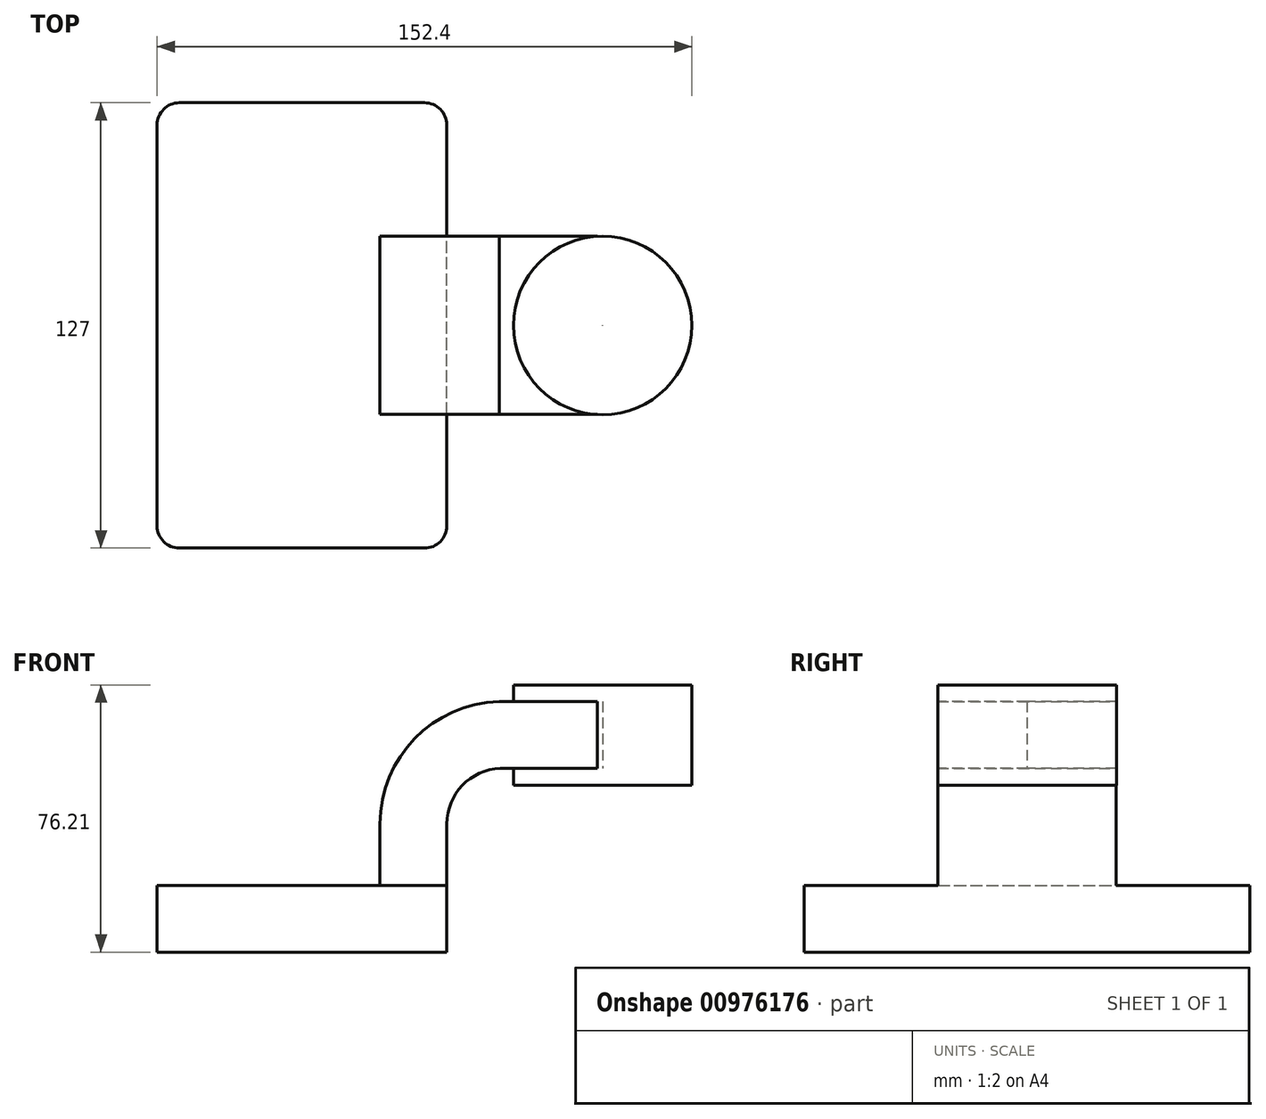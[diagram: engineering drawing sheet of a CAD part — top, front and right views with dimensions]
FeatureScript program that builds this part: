
annotation { "Feature Type Name" : "Feature", "Feature Type Description" : "" }
export const myFeature = defineFeature(function(context is Context, id is Id, definition is map)
    precondition{}
    {
        {
            var Q0;
            Q0=qCreatedBy(makeId("Front.planeOp"),FACE);
            var sketch = newSketch(context, id + "F0", { "sketchPlane" : qUnion([Q0])});
            skLineSegment(sketch, "E0.bottom", {"start": v(41.28, -9.52) * mm, "end": v(-41.27, -9.53) * mm});
            skLineSegment(sketch, "E0.top", {"start": v(41.27, 9.53) * mm, "end": v(-41.28, 9.53) * mm});
            skLineSegment(sketch, "E0.left", {"start": v(41.28, -9.52) * mm, "end": v(41.28, 9.53) * mm});
            skLineSegment(sketch, "E0.right", {"start": v(-41.27, -9.53) * mm, "end": v(-41.28, 9.53) * mm});
            skPoint(sketch, "E0.middle", {"position": v(0, 0) * mm});
            skLineSegment(sketch, "E1.bottom", {"start": v(111.12, 38.1) * mm, "end": v(60.32, 38.1) * mm});
            skLineSegment(sketch, "E1.top", {"start": v(111.12, 66.68) * mm, "end": v(60.32, 66.68) * mm});
            skLineSegment(sketch, "E1.left", {"start": v(111.12, 38.1) * mm, "end": v(111.12, 66.68) * mm});
            skLineSegment(sketch, "E1.right", {"start": v(60.32, 38.1) * mm, "end": v(60.32, 66.68) * mm});
            skPoint(sketch, "E1.middle", {"position": v(85.72, 52.39) * mm});
            skLineSegment(sketch, "E2", {"start": v(41.27, 9.53) * mm, "end": v(41.27, 27.01) * mm});
            skArc(sketch, "E3", {"start": v(41.27, 27.01) * mm, "mid": v(45.7, 38) * mm, "end": v(56.49, 42.88) * mm});
            skLineSegment(sketch, "E4", {"start": v(56.49, 42.88) * mm, "end": v(85.71, 42.88) * mm});
            skLineSegment(sketch, "E5.0", {"start": v(56.17, 61.93) * mm, "end": v(85.71, 61.93) * mm});
            skArc(sketch, "E5.1", {"start": v(22.23, 27.01) * mm, "mid": v(32.1, 51.36) * mm, "end": v(56.17, 61.93) * mm});
            skLineSegment(sketch, "E5.2", {"start": v(22.23, 9.53) * mm, "end": v(22.23, 27.01) * mm});
            skLineSegment(sketch, "E6", {"start": v(85.71, 42.88) * mm, "end": v(85.71, 61.93) * mm});
            skFitSpline(sketch, "E7", {"points": [v(-41.28, 9.53) * mm, v(56.17, 61.93) * mm], "startDerivative": vector(1.72, 146.9) * mm, "endDerivative": vector(113.51, -5.56) * mm});
            skLineSegment(sketch, "E8", {"start": v(85.68, 38.1) * mm, "end": v(85.68, 66.68) * mm});
            skSolve(sketch);
        }
        {
            var Q0;
            Q0=makeQuery(id+"F0.imprint","IMPRINT",FACE,{"disambiguationData":[TD([[makeQuery(id+"F0.imprint","IMPRINT",EDGE,{"derivedFrom":sQuery(id+"F0.wireOp",EDGE,"E0.bottom")}),-1.0]])]});
            extrude(context, id + "F1", {"entities" : qUnion([Q0]), "endBound" : BoundingType.SYMMETRIC, "depth" : 127 * mm, "offsetDistance" : 25.4 * mm});
        }
        {
            var Q0;
            {var subQ1=sQuery(id+"F0.wireOp",EDGE,"E2");Q0=makeQuery(id+"F0.imprint","IMPRINT",FACE,{"disambiguationData":[TD([[makeQuery(id+"F0.imprint","IMPRINT",EDGE,{"derivedFrom":subQ1}),1.0]])]});}
            extrude(context, id + "F2", {"entities" : qUnion([Q0]), "operationType" : NewBodyOperationType.ADD, "endBound" : BoundingType.SYMMETRIC, "depth" : 50.8 * mm, "offsetDistance" : 25.4 * mm});
        }
        {
            var Q0;
            Q0=makeQuery(id+"F0.imprint","IMPRINT",FACE,{"disambiguationData":[TD([[makeQuery(id+"F0.imprint","IMPRINT",EDGE,{"derivedFrom":sQuery(id+"F0.wireOp",EDGE,"E5.1")}),1.0]])]});
            extrude(context, id + "F3", {"entities" : qUnion([Q0]), "operationType" : NewBodyOperationType.ADD, "endBound" : BoundingType.SYMMETRIC, "depth" : 15.88 * mm, "offsetDistance" : 25.4 * mm});
        }
        {
            var Q0;
            {var subQ0=sQuery(id+"F0.wireOp",EDGE,"E1.left");Q0=makeQuery(id+"F0.imprint","IMPRINT",FACE,{"disambiguationData":[TD([[makeQuery(id+"F0.imprint","IMPRINT",EDGE,{"derivedFrom":subQ0}),1.0]])]});}
            var Q1;
            Q1=sQuery(id+"F0.wireOp",EDGE,"E8");
            revolve(context, id + "F4", {"operationType" : NewBodyOperationType.ADD, "surfaceOperationType" : NewSurfaceOperationType.NEW, "entities" : qUnion([Q0]), "axis" : qUnion([Q1]), "revolveType" : RevolveType.FULL});
        }
        {
            var Q0;
            {var subQ0=sQuery(id+"F0.wireOp",EDGE,"E4");var subQ1=sQuery(id+"F0.wireOp",EDGE,"E1.right");var subQ2=makeQuery(id+"F0.imprint","INTERSECT",VERTEX,{"derivedFrom":[subQ1,subQ0]});Q0=makeQuery(id+"F0.imprint","IMPRINT",FACE,{"disambiguationData":[TD([[makeQuery(id+"F0.imprint","IMPRINT",EDGE,{"disambiguationData":[TD([[subQ2,-1.0]])],"derivedFrom":subQ1}),-1.0]])]});}
            extrude(context, id + "F5", {"entities" : qUnion([Q0]), "operationType" : NewBodyOperationType.ADD, "endBound" : BoundingType.SYMMETRIC, "depth" : 50.8 * mm, "offsetDistance" : 25.4 * mm});
        }
        {
            var Q0;
            Q0=makeQuery(id+"F1.opExtrude","CAP_EDGE",EDGE,{"disambiguationData":[OSD([sQuery(id+"F0.wireOp",EDGE,"E0.left")])],"isStart":false});
            var Q1;
            Q1=makeQuery(id+"F1.opExtrude","CAP_EDGE",EDGE,{"disambiguationData":[OSD([sQuery(id+"F0.wireOp",EDGE,"E0.right")])],"isStart":false});
            var Q2;
            Q2=makeQuery(id+"F1.opExtrude","CAP_EDGE",EDGE,{"disambiguationData":[OSD([sQuery(id+"F0.wireOp",EDGE,"E0.left")])],"isStart":true});
            var Q3;
            Q3=makeQuery(id+"F1.opExtrude","CAP_EDGE",EDGE,{"disambiguationData":[OSD([sQuery(id+"F0.wireOp",EDGE,"E0.right")])],"isStart":true});
            fillet(context, id + "F6", {"entities" : qUnion([Q0, Q1, Q2, Q3]), "radius" : 6.35 * mm, "tangentPropagation" : true, "allowEdgeOverflow" : false});
        }
    });
